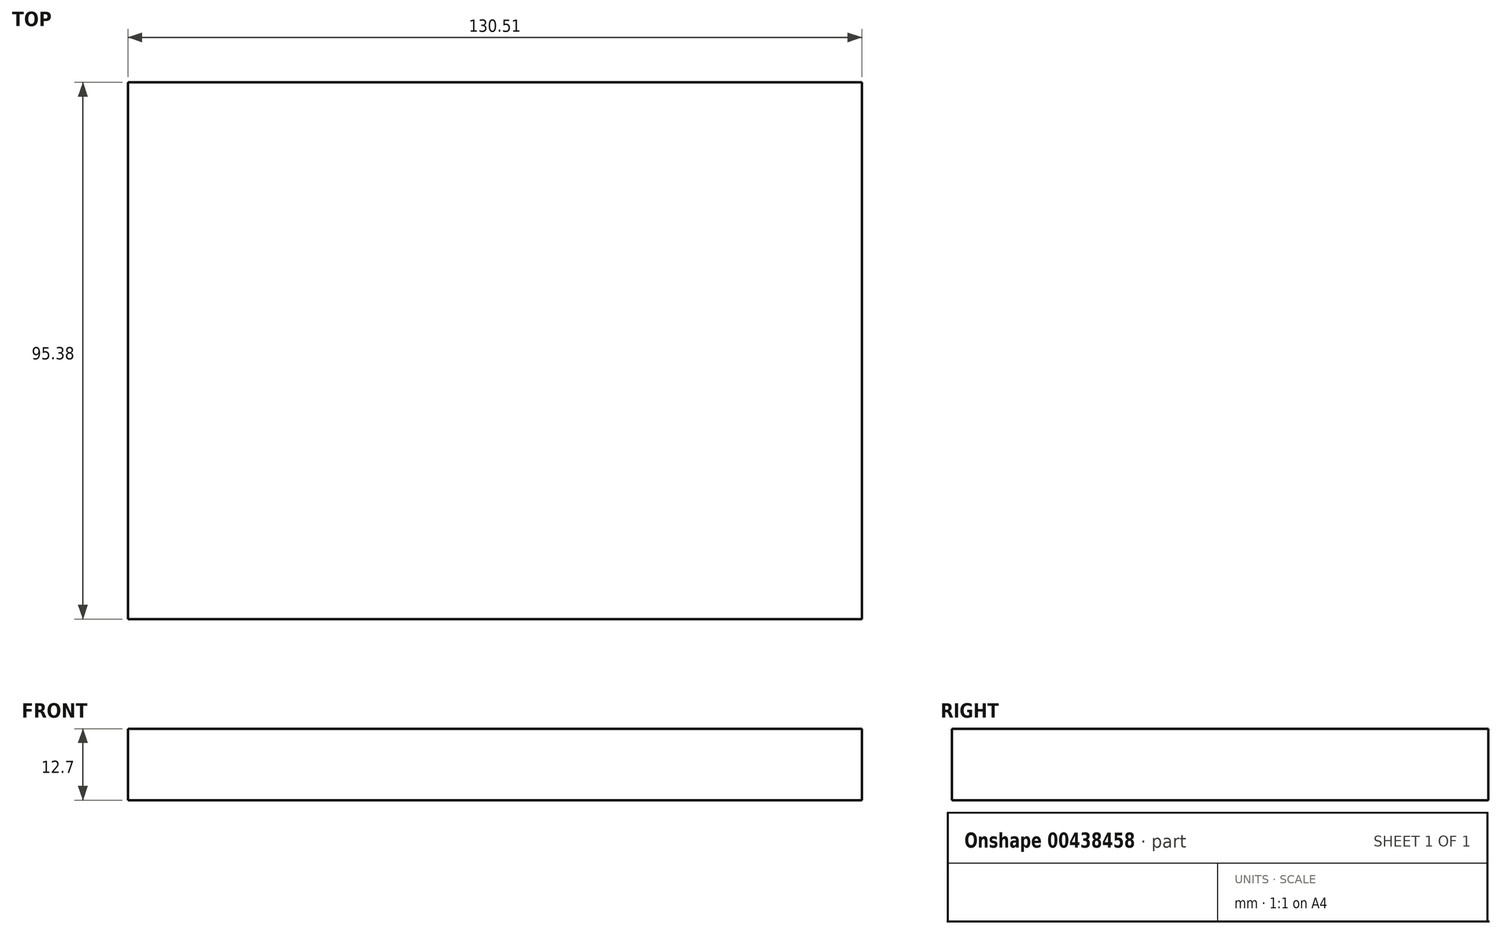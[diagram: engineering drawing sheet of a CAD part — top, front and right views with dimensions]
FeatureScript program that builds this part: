
annotation { "Feature Type Name" : "Feature", "Feature Type Description" : "" }
export const myFeature = defineFeature(function(context is Context, id is Id, definition is map)
    precondition{}
    {
        {
            var Q0;
            Q0=qCreatedBy(makeId("Top.planeOp"),FACE);
            var sketch = newSketch(context, id + "F0", { "sketchPlane" : qUnion([Q0])});
            skLineSegment(sketch, "E0.bottom", {"start": v(-63.78, -51.47) * mm, "end": v(66.73, -51.47) * mm});
            skLineSegment(sketch, "E0.top", {"start": v(-63.78, 43.91) * mm, "end": v(66.73, 43.91) * mm});
            skLineSegment(sketch, "E0.left", {"start": v(-63.78, -51.47) * mm, "end": v(-63.78, 43.91) * mm});
            skLineSegment(sketch, "E0.right", {"start": v(66.73, -51.47) * mm, "end": v(66.73, 43.91) * mm});
            skSolve(sketch);
        }
        {
            var Q0;
            Q0 = qSketchRegion(id + "F0", true);
            extrude(context, id + "F1", {"entities" : qUnion([Q0]), "depth" : 12.7 * mm});
        }
    });
